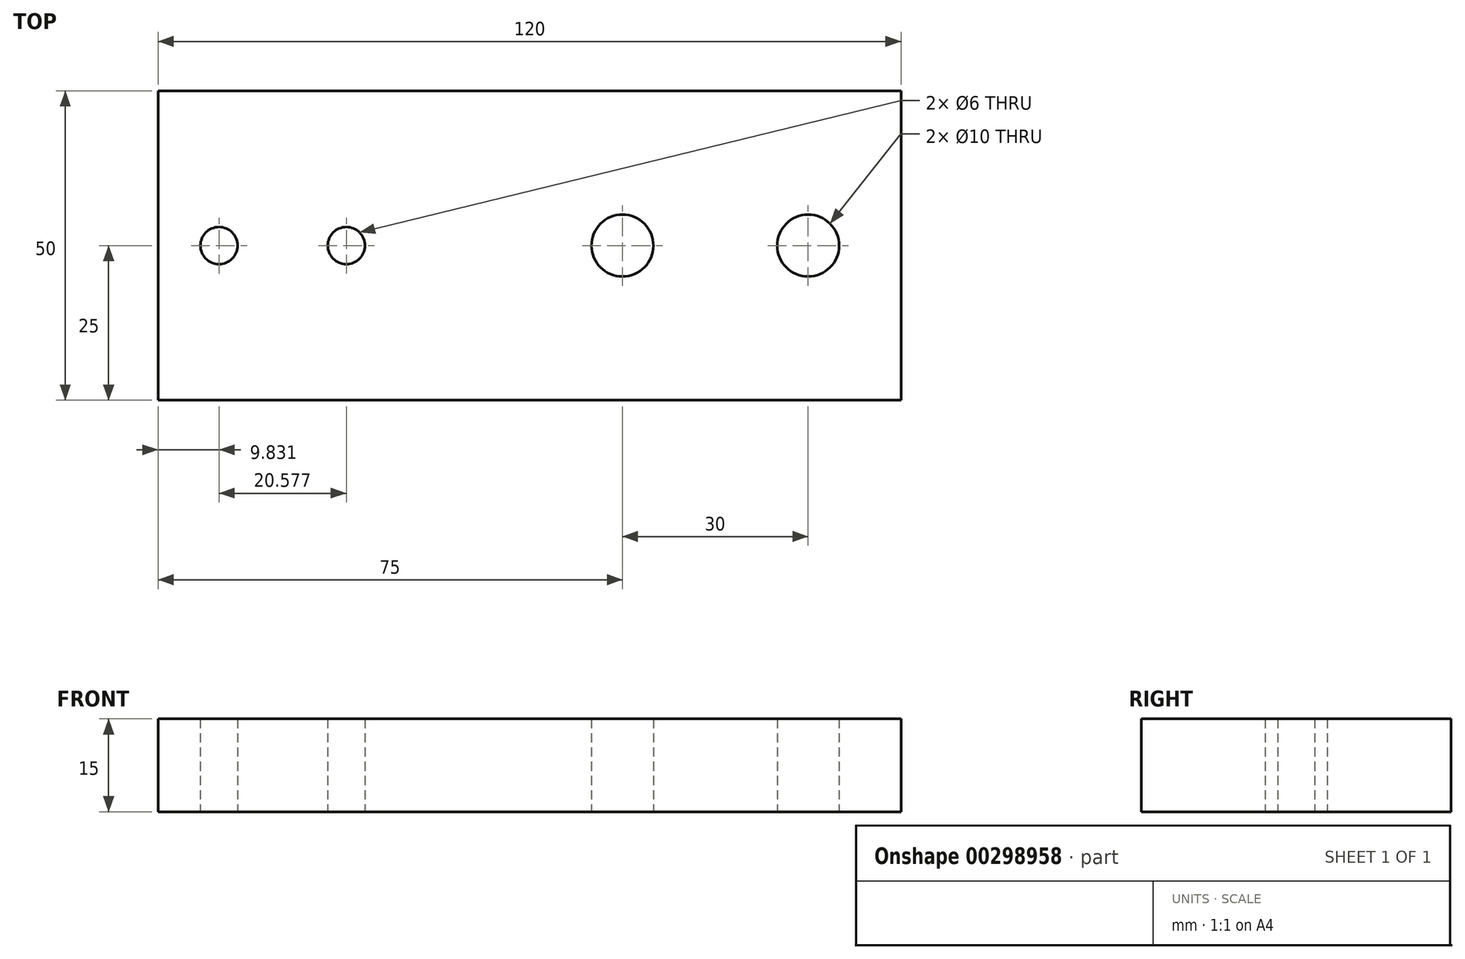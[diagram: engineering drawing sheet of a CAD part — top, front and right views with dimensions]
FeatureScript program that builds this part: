
annotation { "Feature Type Name" : "Feature", "Feature Type Description" : "" }
export const myFeature = defineFeature(function(context is Context, id is Id, definition is map)
    precondition{}
    {
        {
            var Q0;
            Q0=qCreatedBy(makeId("Top.planeOp"),FACE);
            var sketch = newSketch(context, id + "F0", { "sketchPlane" : qUnion([Q0])});
            skLineSegment(sketch, "E0.bottom", {"start": v(60, 25) * mm, "end": v(-60, 25) * mm});
            skLineSegment(sketch, "E0.top", {"start": v(60, -25) * mm, "end": v(-60, -25) * mm});
            skLineSegment(sketch, "E0.left", {"start": v(60, 25) * mm, "end": v(60, -25) * mm});
            skLineSegment(sketch, "E0.right", {"start": v(-60, 25) * mm, "end": v(-60, -25) * mm});
            skPoint(sketch, "E0.middle", {"position": v(0, 0) * mm});
            skCircle(sketch, "E1", {"center": v(45, 0) * mm, "radius": 5 * mm});
            skCircle(sketch, "E2", {"center": v(15, 0) * mm, "radius": 5 * mm});
            skCircle(sketch, "E3", {"center": v(-50.17, 0) * mm, "radius": 3 * mm});
            skCircle(sketch, "E4", {"center": v(-29.6, 0) * mm, "radius": 3 * mm});
            skSolve(sketch);
        }
        {
            var Q0;
            Q0 = qSketchRegion(id + "F0", true);
            extrude(context, id + "F1", {"entities" : qUnion([Q0]), "depth" : 15 * mm});
        }
    });
